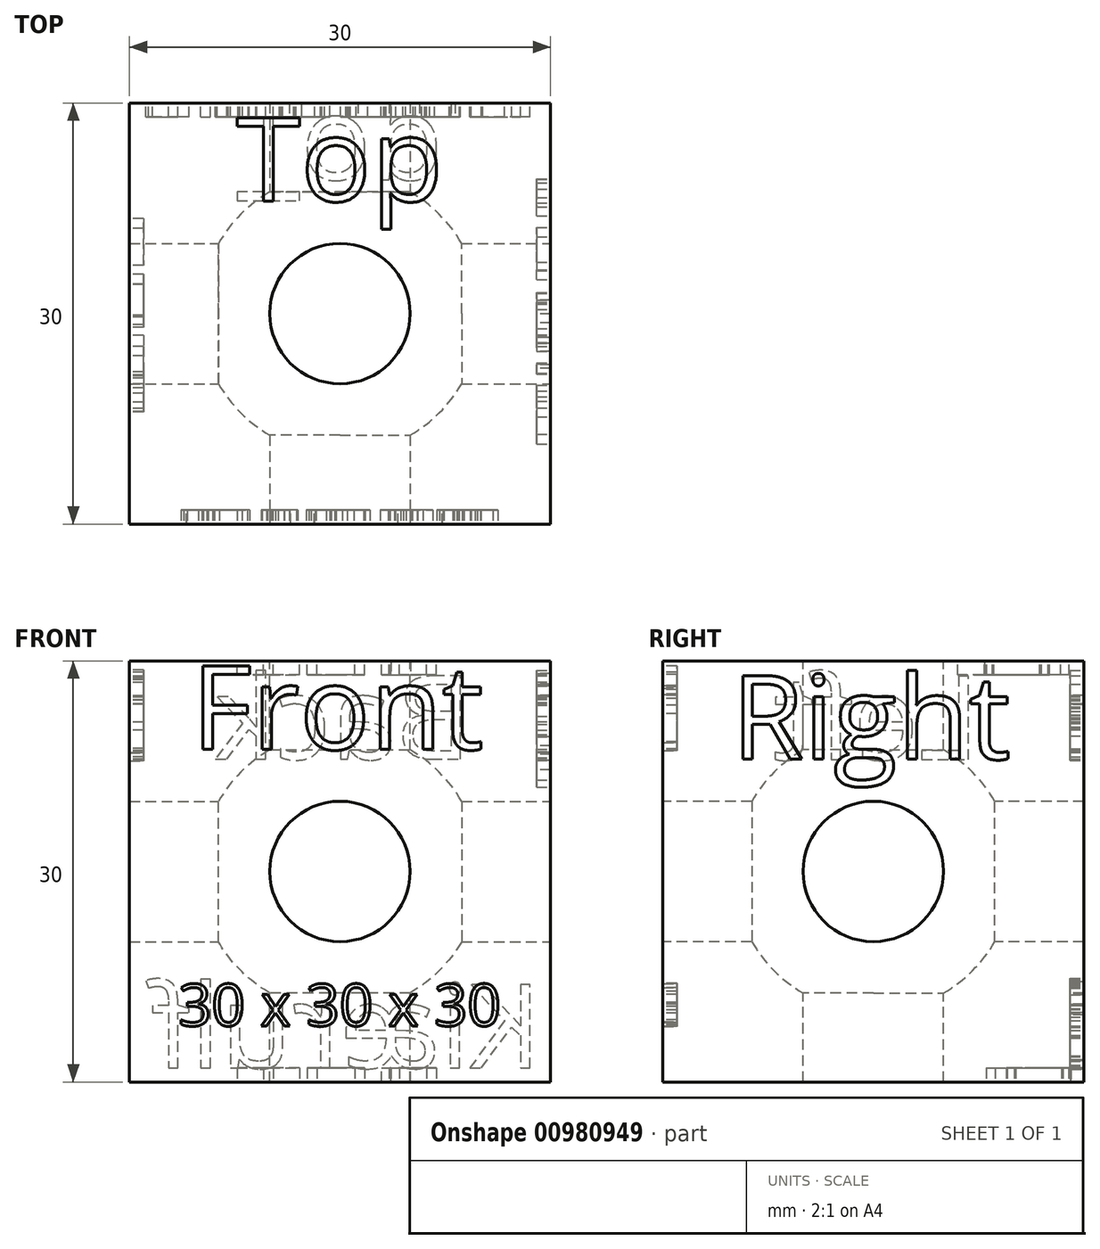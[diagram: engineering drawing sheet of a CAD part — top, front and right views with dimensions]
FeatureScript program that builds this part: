
annotation { "Feature Type Name" : "Feature", "Feature Type Description" : "" }
export const myFeature = defineFeature(function(context is Context, id is Id, definition is map)
    precondition{}
    {
        {
            var Q0;
            Q0=qCreatedBy(makeId("Front.planeOp"),FACE);
            var sketch = newSketch(context, id + "F0", { "sketchPlane" : qUnion([Q0])});
            skLineSegment(sketch, "E0.bottom", {"start": v(15, 15) * mm, "end": v(-15, 15) * mm});
            skLineSegment(sketch, "E0.top", {"start": v(15, -15) * mm, "end": v(-15, -15) * mm});
            skLineSegment(sketch, "E0.left", {"start": v(15, 15) * mm, "end": v(15, -15) * mm});
            skLineSegment(sketch, "E0.right", {"start": v(-15, 15) * mm, "end": v(-15, -15) * mm});
            skPoint(sketch, "E0.middle", {"position": v(0, 0) * mm});
            skSolve(sketch);
        }
        {
            var Q0;
            Q0 = qSketchRegion(id + "F0", true);
            extrude(context, id + "F1", {"entities" : qUnion([Q0]), "endBound" : BoundingType.SYMMETRIC, "oppositeDirection" : true, "depth" : 30 * mm, "offsetDistance" : 25 * mm});
        }
        {
            var Q0;
            Q0=makeQuery(id+"F1.opExtrude","CAP_FACE",FACE,{"disambiguationData":[OSD([sQuery(id+"F0.wireOp",EDGE,"E0.bottom"),sQuery(id+"F0.wireOp",EDGE,"E0.top"),sQuery(id+"F0.wireOp",EDGE,"E0.left"),sQuery(id+"F0.wireOp",EDGE,"E0.right")])],"isStart":true});
            var sketch = newSketch(context, id + "F2", { "sketchPlane" : qUnion([Q0])});
            skCircle(sketch, "E1", {"center": v(0, 0) * mm, "radius": 5 * mm});
            skSolve(sketch);
        }
        {
            var Q0;
            Q0 = qSketchRegion(id + "F2", true);
            extrude(context, id + "F3", {"entities" : qUnion([Q0]), "operationType" : NewBodyOperationType.REMOVE, "endBound" : BoundingType.THROUGH_ALL, "oppositeDirection" : true, "depth" : 25 * mm, "offsetDistance" : 25 * mm});
        }
        {
            var Q0;
            Q0=makeQuery(id+"F1.opExtrude","SWEPT_FACE",FACE,{"disambiguationData":[OSD([sQuery(id+"F0.wireOp",EDGE,"E0.left")])]});
            var sketch = newSketch(context, id + "F4", { "sketchPlane" : qUnion([Q0])});
            skCircle(sketch, "E2", {"center": v(0, 0) * mm, "radius": 5 * mm});
            skSolve(sketch);
        }
        {
            var Q0;
            Q0 = qSketchRegion(id + "F4", true);
            extrude(context, id + "F5", {"entities" : qUnion([Q0]), "operationType" : NewBodyOperationType.REMOVE, "endBound" : BoundingType.THROUGH_ALL, "oppositeDirection" : true, "depth" : 25 * mm, "offsetDistance" : 25 * mm});
        }
        {
            var Q0;
            Q0=makeQuery(id+"F1.opExtrude","SWEPT_FACE",FACE,{"disambiguationData":[OSD([sQuery(id+"F0.wireOp",EDGE,"E0.bottom")])]});
            var sketch = newSketch(context, id + "F6", { "sketchPlane" : qUnion([Q0])});
            skCircle(sketch, "E3", {"center": v(0, 0) * mm, "radius": 5 * mm});
            skSolve(sketch);
        }
        {
            var Q0;
            Q0 = qSketchRegion(id + "F6", true);
            extrude(context, id + "F7", {"entities" : qUnion([Q0]), "operationType" : NewBodyOperationType.REMOVE, "endBound" : BoundingType.THROUGH_ALL, "oppositeDirection" : true, "depth" : 25 * mm, "offsetDistance" : 25 * mm});
        }
        {
            var Q0;
            Q0=qCreatedBy(makeId("Front.planeOp"),FACE);
            var sketch = newSketch(context, id + "F8", { "sketchPlane" : qUnion([Q0])});
            skArc(sketch, "E4", {"start": v(10, 0) * mm, "mid": v(0, 10) * mm, "end": v(-10, 0) * mm});
            skLineSegment(sketch, "E5", {"start": v(20.65, 0) * mm, "end": v(-22.52, 0) * mm, "construction": true});
            skLineSegment(sketch, "E6", {"start": v(10, 0) * mm, "end": v(-10, 0) * mm});
            skSolve(sketch);
        }
        {
            var Q0;
            Q0=makeQuery(id+"F8.imprint","IMPRINT",FACE,{"disambiguationData":[TD([[makeQuery(id+"F8.imprint","IMPRINT",EDGE,{"derivedFrom":sQuery(id+"F8.wireOp",EDGE,"E4")}),1.0]])]});
            var Q1;
            Q1=sQuery(id+"F8.wireOp",EDGE,"E5");
            revolve(context, id + "F9", {"operationType" : NewBodyOperationType.REMOVE, "surfaceOperationType" : NewSurfaceOperationType.NEW, "entities" : qUnion([Q0]), "axis" : qUnion([Q1]), "revolveType" : RevolveType.FULL, "oppositeDirection" : true});
        }
        {
            var Q0;
            Q0=makeQuery(id+"F1.opExtrude","CAP_FACE",FACE,{"disambiguationData":[OSD([sQuery(id+"F0.wireOp",EDGE,"E0.bottom"),sQuery(id+"F0.wireOp",EDGE,"E0.top"),sQuery(id+"F0.wireOp",EDGE,"E0.left"),sQuery(id+"F0.wireOp",EDGE,"E0.right")])],"isStart":true});
            var sketch = newSketch(context, id + "F10", { "sketchPlane" : qUnion([Q0])});
            skText(sketch, "E7", { "text": "Front", "fontName": "OpenSans-Regular.ttf"});
            const initialGuessF10  = {"E7": [-0.01058, 0.00869, 1, 0, 0.006]};
            skSetInitialGuess(sketch, initialGuessF10);
            skSolve(sketch);
        }
        {
            var Q0;
            Q0 = qSketchRegion(id + "F10", true);
            extrude(context, id + "F11", {"entities" : qUnion([Q0]), "operationType" : NewBodyOperationType.REMOVE, "oppositeDirection" : true, "depth" : 1 * mm, "offsetDistance" : 25 * mm});
        }
        {
            var Q0;
            Q0=makeQuery(id+"F1.opExtrude","SWEPT_FACE",FACE,{"disambiguationData":[OSD([sQuery(id+"F0.wireOp",EDGE,"E0.bottom")])]});
            var sketch = newSketch(context, id + "F12", { "sketchPlane" : qUnion([Q0])});
            skText(sketch, "E8", { "text": "Top", "fontName": "OpenSans-Regular.ttf"});
            const initialGuessF12  = {"E8": [-0.00741, 0.008, 1, 0, 0.006]};
            skSetInitialGuess(sketch, initialGuessF12);
            skSolve(sketch);
        }
        {
            var Q0;
            Q0 = qSketchRegion(id + "F12", true);
            extrude(context, id + "F13", {"entities" : qUnion([Q0]), "operationType" : NewBodyOperationType.REMOVE, "oppositeDirection" : true, "depth" : 1 * mm, "offsetDistance" : 25 * mm});
        }
        {
            var Q0;
            Q0=makeQuery(id+"F1.opExtrude","SWEPT_FACE",FACE,{"disambiguationData":[OSD([sQuery(id+"F0.wireOp",EDGE,"E0.right")])]});
            var sketch = newSketch(context, id + "F14", { "sketchPlane" : qUnion([Q0])});
            skText(sketch, "E9", { "text": "Left", "fontName": "OpenSans-Regular.ttf"});
            const initialGuessF14  = {"E9": [-0.00758, 0.00797, 1, 0, 0.006]};
            skSetInitialGuess(sketch, initialGuessF14);
            skSolve(sketch);
        }
        {
            var Q0;
            Q0 = qSketchRegion(id + "F14", true);
            extrude(context, id + "F15", {"entities" : qUnion([Q0]), "operationType" : NewBodyOperationType.REMOVE, "oppositeDirection" : true, "depth" : 1 * mm, "offsetDistance" : 25 * mm});
        }
        {
            var Q0;
            Q0=makeQuery(id+"F1.opExtrude","SWEPT_FACE",FACE,{"disambiguationData":[OSD([sQuery(id+"F0.wireOp",EDGE,"E0.left")])]});
            var sketch = newSketch(context, id + "F16", { "sketchPlane" : qUnion([Q0])});
            skText(sketch, "E10", { "text": "Right", "fontName": "OpenSans-Regular.ttf"});
            const initialGuessF16  = {"E10": [-0.01012, 0.008, 1, 0, 0.006]};
            skSetInitialGuess(sketch, initialGuessF16);
            skSolve(sketch);
        }
        {
            var Q0;
            Q0 = qSketchRegion(id + "F16", true);
            extrude(context, id + "F17", {"entities" : qUnion([Q0]), "operationType" : NewBodyOperationType.REMOVE, "oppositeDirection" : true, "depth" : 1 * mm, "offsetDistance" : 25 * mm});
        }
        {
            var Q0;
            Q0=makeQuery(id+"F1.opExtrude","CAP_FACE",FACE,{"disambiguationData":[OSD([sQuery(id+"F0.wireOp",EDGE,"E0.bottom"),sQuery(id+"F0.wireOp",EDGE,"E0.top"),sQuery(id+"F0.wireOp",EDGE,"E0.left"),sQuery(id+"F0.wireOp",EDGE,"E0.right")])],"isStart":false});
            var sketch = newSketch(context, id + "F18", { "sketchPlane" : qUnion([Q0])});
            skText(sketch, "E11", { "text": "Back", "fontName": "OpenSans-Regular.ttf"});
            const initialGuessF18  = {"E11": [-0.00941, 0.008, 1, 0, 0.006]};
            skSetInitialGuess(sketch, initialGuessF18);
            skSolve(sketch);
        }
        {
            var Q0;
            Q0 = qSketchRegion(id + "F18", true);
            extrude(context, id + "F19", {"entities" : qUnion([Q0]), "operationType" : NewBodyOperationType.REMOVE, "oppositeDirection" : true, "depth" : 1 * mm, "offsetDistance" : 25 * mm});
        }
        {
            var Q0;
            Q0=makeQuery(id+"F1.opExtrude","SWEPT_FACE",FACE,{"disambiguationData":[OSD([sQuery(id+"F0.wireOp",EDGE,"E0.top")])]});
            var sketch = newSketch(context, id + "F20", { "sketchPlane" : qUnion([Q0])});
            skText(sketch, "E12", { "text": "Top", "fontName": "OpenSans-Regular.ttf"});
            const initialGuessF20  = {"E12": [-0.00741, -0.014, 1, 0, 0.006]};
            skSetInitialGuess(sketch, initialGuessF20);
            skSolve(sketch);
        }
        {
            var Q0;
            Q0 = qSketchRegion(id + "F20", true);
            extrude(context, id + "F21", {"entities" : qUnion([Q0]), "operationType" : NewBodyOperationType.REMOVE, "oppositeDirection" : true, "depth" : 1 * mm, "offsetDistance" : 25 * mm});
        }
        {
            var Q0;
            {var subQ0=sQuery(id+"F0.wireOp",EDGE,"E0.bottom");var subQ1=sQuery(id+"F0.wireOp",EDGE,"E0.right");var subQ2=sQuery(id+"F0.wireOp",EDGE,"E0.top");var subQ3=sQuery(id+"F0.wireOp",EDGE,"E0.left");Q0=makeQuery(id+"F11.boolean.opBoolean","SPLIT",FACE,{"disambiguationData":[TD([makeQuery(id+"F1.opExtrude","SWEPT_FACE",FACE,{"disambiguationData":[OSD([subQ0])]})])],"derivedFrom":makeQuery(id+"F1.opExtrude","CAP_FACE",FACE,{"disambiguationData":[OSD([subQ0,subQ2,subQ3,subQ1])],"isStart":true})});}
            var sketch = newSketch(context, id + "F22", { "sketchPlane" : qUnion([Q0])});
            skText(sketch, "E13", { "text": "30 x 30 x 30", "fontName": "OpenSans-Regular.ttf"});
            const initialGuessF22  = {"E13": [-0.01153, -0.011, 1, 0, 0.003]};
            skSetInitialGuess(sketch, initialGuessF22);
            skSolve(sketch);
        }
        {
            var Q0;
            Q0 = qSketchRegion(id + "F22", true);
            extrude(context, id + "F23", {"entities" : qUnion([Q0]), "operationType" : NewBodyOperationType.REMOVE, "oppositeDirection" : true, "depth" : 1 * mm, "offsetDistance" : 25 * mm});
        }
        {
            var Q0;
            {var subQ0=sQuery(id+"F0.wireOp",EDGE,"E0.bottom");var subQ1=sQuery(id+"F0.wireOp",EDGE,"E0.right");var subQ2=sQuery(id+"F0.wireOp",EDGE,"E0.top");var subQ3=sQuery(id+"F0.wireOp",EDGE,"E0.left");Q0=makeQuery(id+"F19.boolean.opBoolean","SPLIT",FACE,{"disambiguationData":[TD([makeQuery(id+"F1.opExtrude","SWEPT_FACE",FACE,{"disambiguationData":[OSD([subQ0])]})])],"derivedFrom":makeQuery(id+"F1.opExtrude","CAP_FACE",FACE,{"disambiguationData":[OSD([subQ0,subQ2,subQ3,subQ1])],"isStart":false})});}
            var sketch = newSketch(context, id + "F24", { "sketchPlane" : qUnion([Q0])});
            skText(sketch, "E14", { "text": "Kiærulf", "fontName": "OpenSans-Regular.ttf"});
            const initialGuessF24  = {"E14": [-0.01436, -0.014, 1, 0, 0.006]};
            skSetInitialGuess(sketch, initialGuessF24);
            skSolve(sketch);
        }
        {
            var Q0;
            Q0 = qSketchRegion(id + "F24", true);
            extrude(context, id + "F25", {"entities" : qUnion([Q0]), "operationType" : NewBodyOperationType.REMOVE, "oppositeDirection" : true, "depth" : 1 * mm, "offsetDistance" : 25 * mm});
        }
    });
